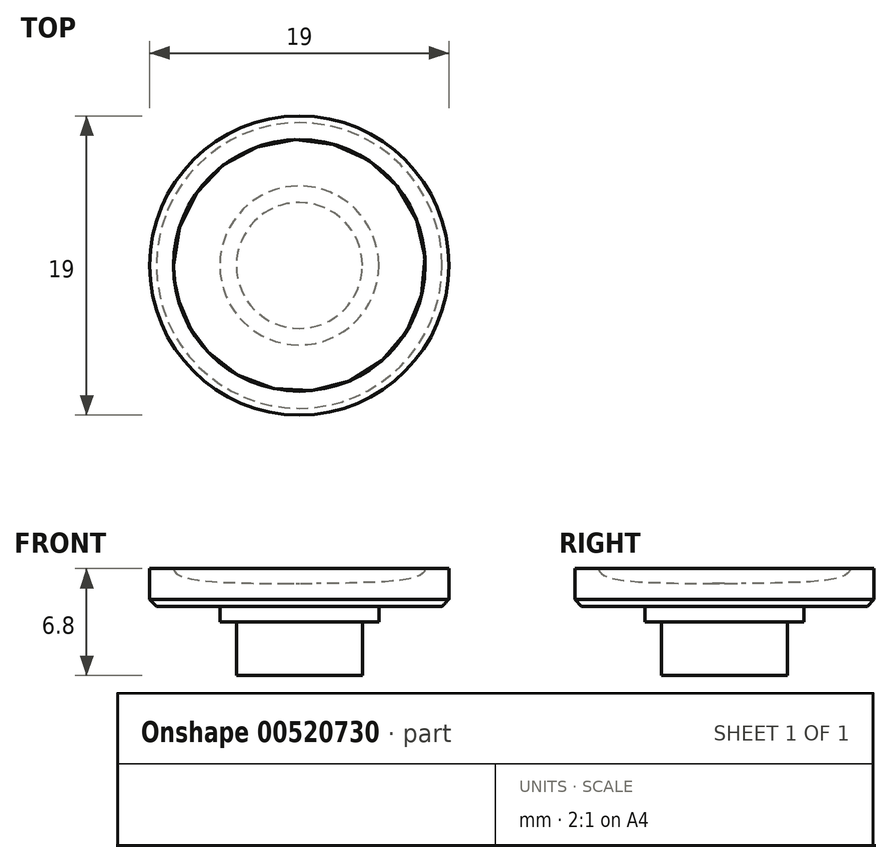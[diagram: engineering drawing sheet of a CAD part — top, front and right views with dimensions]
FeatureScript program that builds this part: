
annotation { "Feature Type Name" : "Feature", "Feature Type Description" : "" }
export const myFeature = defineFeature(function(context is Context, id is Id, definition is map)
    precondition{}
    {
        {
            var Q0;
            Q0=qCreatedBy(makeId("Front.planeOp"),FACE);
            var sketch = newSketch(context, id + "F0", { "sketchPlane" : qUnion([Q0])});
            skLineSegment(sketch, "E0", {"start": v(-9.5, 2.4) * mm, "end": v(-8, 2.4) * mm});
            skLineSegment(sketch, "E1", {"start": v(-9.5, 2.4) * mm, "end": v(-9.5, 0.45) * mm});
            skLineSegment(sketch, "E2", {"start": v(-9.07, 0) * mm, "end": v(0, 0) * mm});
            skLineSegment(sketch, "E3", {"start": v(-9.5, 0.45) * mm, "end": v(-9.07, 0) * mm});
            skFitSpline(sketch, "E4", {"points": [v(-8, 2.4) * mm, v(-3.86, 1.5) * mm, v(0, 1.45) * mm], "startDerivative": vector(0, -4.6) * mm, "endDerivative": vector(11, 0.1) * mm});
            skLineSegment(sketch, "E5", {"start": v(0, 0) * mm, "end": v(0, 1.45) * mm});
            skLineSegment(sketch, "E6", {"start": v(0, 2.9) * mm, "end": v(0, 0) * mm, "construction": true});
            skSolve(sketch);
        }
        {
            var Q0;
            Q0 = qSketchRegion(id + "F0", true);
            var Q1;
            Q1=sQuery(id+"F0.wireOp",EDGE,"E6");
            revolve(context, id + "F1", {"entities" : qUnion([Q0]), "axis" : qUnion([Q1]), "revolveType" : RevolveType.FULL});
        }
        {
            var Q0;
            Q0=makeQuery(id+"F1.opRevolve","SWEPT_FACE",FACE,{"disambiguationData":[OSD([sQuery(id+"F0.wireOp",EDGE,"E2")])]});
            var sketch = newSketch(context, id + "F2", { "sketchPlane" : qUnion([Q0])});
            skCircle(sketch, "E7", {"center": v(0, 0) * mm, "radius": 5.05 * mm});
            skSolve(sketch);
        }
        {
            var Q0;
            Q0 = qSketchRegion(id + "F2", true);
            extrude(context, id + "F3", {"entities" : qUnion([Q0]), "operationType" : NewBodyOperationType.ADD, "depth" : 1 * mm, "offsetDistance" : 25 * mm});
        }
        {
            var Q0;
            Q0=makeQuery(id+"F3.opExtrude","CAP_FACE",FACE,{"disambiguationData":[OSD([sQuery(id+"F2.wireOp",EDGE,"E7")])],"isStart":false});
            var sketch = newSketch(context, id + "F4", { "sketchPlane" : qUnion([Q0])});
            skCircle(sketch, "E8", {"center": v(0, 0) * mm, "radius": 4 * mm});
            skSolve(sketch);
        }
        {
            var Q0;
            Q0 = qSketchRegion(id + "F4", true);
            extrude(context, id + "F5", {"entities" : qUnion([Q0]), "operationType" : NewBodyOperationType.ADD, "depth" : 3.4 * mm, "offsetDistance" : 25 * mm});
        }
    });
